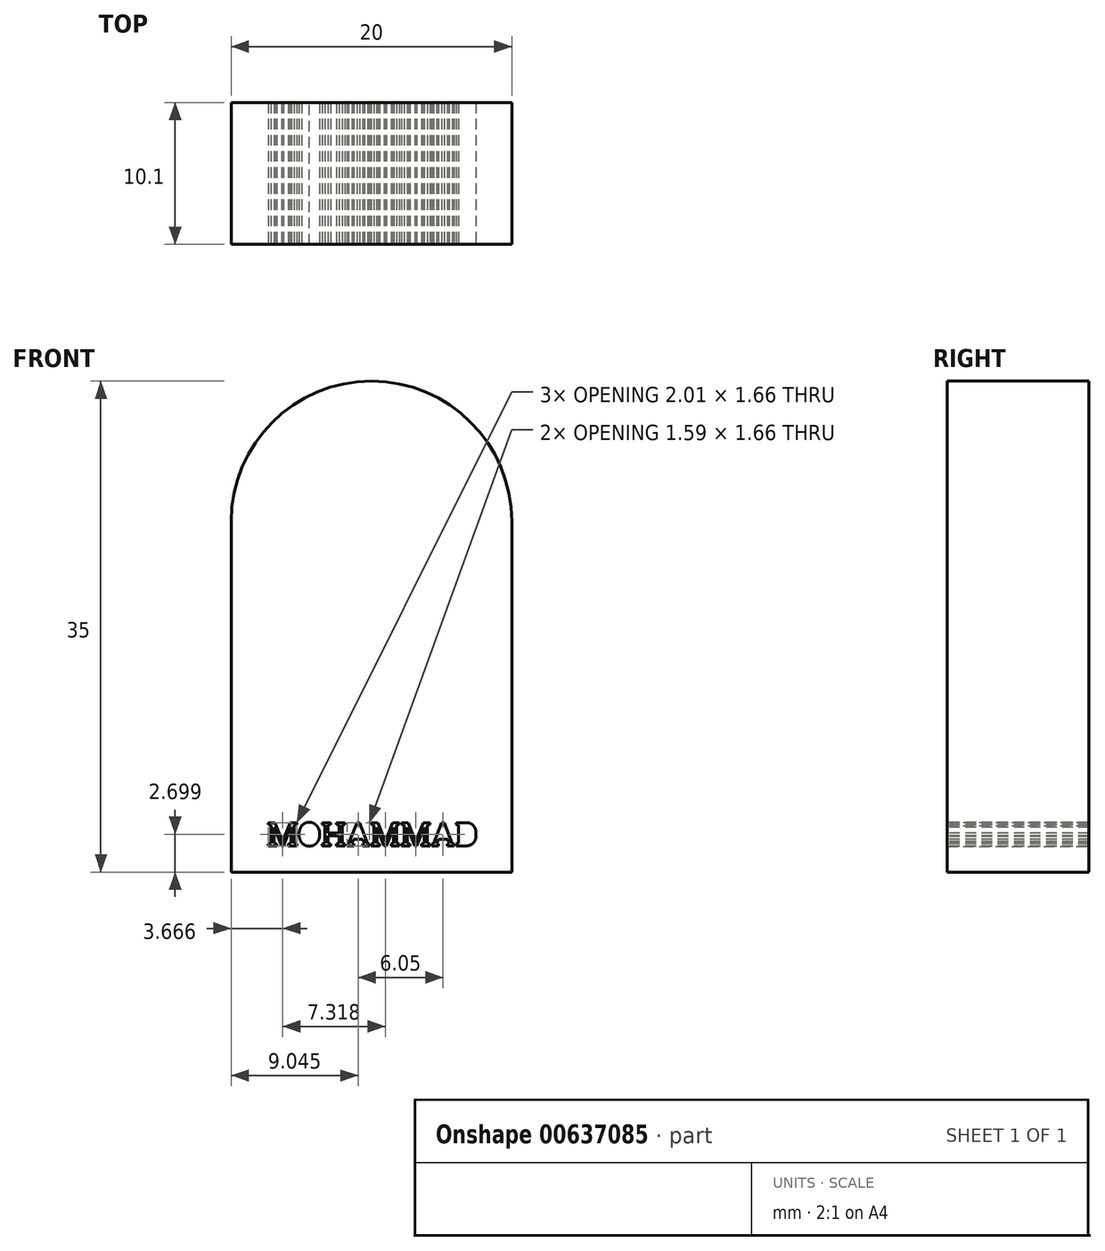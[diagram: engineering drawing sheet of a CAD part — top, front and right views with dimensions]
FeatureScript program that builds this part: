
annotation { "Feature Type Name" : "Feature", "Feature Type Description" : "" }
export const myFeature = defineFeature(function(context is Context, id is Id, definition is map)
    precondition{}
    {
        {
            var Q0;
            Q0=qCreatedBy(makeId("Front.planeOp"),FACE);
            var sketch = newSketch(context, id + "F0", { "sketchPlane" : qUnion([Q0])});
            skText(sketch, "E0", { "text": "MOHAMMAD", "fontName": "RobotoSlab-Regular.ttf"});
            skLineSegment(sketch, "E1.bottom", {"start": v(10, -12.5) * mm, "end": v(-10, -12.5) * mm});
            skLineSegment(sketch, "E1.left", {"start": v(10, -12.5) * mm, "end": v(10, 12.5) * mm});
            skLineSegment(sketch, "E1.right", {"start": v(-10, -12.5) * mm, "end": v(-10, 12.5) * mm});
            skPoint(sketch, "E1.middle", {"position": v(0, 0) * mm});
            skArc(sketch, "E2", {"start": v(10, 12.5) * mm, "mid": v(0, 22.5) * mm, "end": v(-10, 12.5) * mm});
            skLineSegment(sketch, "E3", {"start": v(-10, -12.5) * mm, "end": v(-10, -17.37) * mm});
            skLineSegment(sketch, "E4", {"start": v(-10, -17.37) * mm, "end": v(10, -17.37) * mm});
            skLineSegment(sketch, "E5", {"start": v(10, -17.37) * mm, "end": v(10, -12.5) * mm});
            const initialGuessF0  = {"E0": [-0.00742, -0.01063, 1, 0, 0.00168]};
            skSetInitialGuess(sketch, initialGuessF0);
            skSolve(sketch);
        }
        {
            var Q0;
            Q0=makeQuery(id+"F0.imprint","IMPRINT",FACE,{"disambiguationData":[TD([[makeQuery(id+"F0.imprint","IMPRINT",EDGE,{"derivedFrom":sQuery(id+"F0.wireOp",EDGE,"E0.sketch_text.stroke-0")}),1.0]])]});
            extrude(context, id + "F1", {"entities" : qUnion([Q0]), "oppositeDirection" : true, "depth" : 10.1 * mm, "offsetDistance" : 25 * mm});
        }
    });
